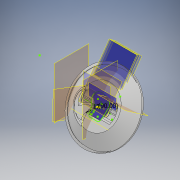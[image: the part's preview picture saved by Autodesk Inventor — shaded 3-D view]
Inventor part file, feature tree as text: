
AUTODESK INVENTOR PART (.ipt)
format: ipt  version: 2018 (Build 220112000, 112)  size: 3,591,168 bytes
history: native  units: mm
features: sketch x139, extrude x124, fillet x51, plane x14, revolve x4, hole x1, direct_edit x1, other x1
ambient origin geometry x8: Origin, YZ Plane, XZ Plane, XY Plane, X Axis, Y Axis, Z Axis, Center Point
bodies: Body1 (feature_tree)
feature tree (335):
  plane  "Work Plane5"
  sketch  "Sketch28"  dims[d118=18.7mm d119=0.0mm d120=0.9mm d121=0.0mm]
  extrude  "Extrusion21"  Depth=0.9mm TaperAngle=0.0deg
  plane  "Work Plane4"
  extrude  "Extrusion22"  Depth=3.8mm
  extrude  "Extrusion23"  Depth=46.7mm
  plane  "Work Plane3"
  hole  "Hole6"  [1 undecoded]
  extrude  "Extrusion27"  Depth=3.8mm
  extrude  "Extrusion28"  Depth=32.03mm
  extrude  "Extrusion30"  Depth=10.0mm TaperAngle=0.0deg
  extrude  "Extrusion31"  Depth=16.3mm TaperAngle=0.0deg
  sketch  "Sketch56"  dims[d188=16.3mm d189=0.0mm d190=16.3mm d191=0.0mm]
  sketch  "Sketch57"  dims[d192=16.3mm d193=0.0mm d194=16.3mm d195=0.0mm]
  extrude  "Extrusion33"  Depth=16.3mm TaperAngle=0.0deg
  extrude  "Extrusion34"  Depth=16.3mm TaperAngle=0.0deg
  extrude  "Extrusion35"  Depth=15.9mm TaperAngle=0.0deg
  extrude  "Extrusion36"  Depth=15.9mm TaperAngle=0.0deg
  extrude  "Extrusion37"  TaperAngle=90.0deg  [1 undecoded]
  extrude  "Extrusion38"  TaperAngle=0.0deg  [1 undecoded]
  extrude  "Extrusion39"  Depth=0.2mm TaperAngle=0.0deg
  extrude  "Extrusion40"  Depth=3.17mm
  extrude  "Extrusion41"  Depth=6.1mm
  sketch  "Sketch68"  dims[d251=10.0mm d252=0.0mm d253=3.91mm d254=0.0mm]
  sketch  "Sketch69"  dims[d255=0.0mm d256=0.0mm d257=3.91mm d258=0.0mm]
  extrude  "Extrusion42"  Depth=0.8mm TaperAngle=0.0deg
  extrude  "Extrusion43"  TaperAngle=0.0deg  [1 undecoded]
  extrude  "Extrusion45"  Depth=10.0mm TaperAngle=0.0deg
  extrude  "Extrusion47"  Depth=3.91mm TaperAngle=0.0deg
  extrude  "Extrusion48"  Depth=0.6mm TaperAngle=0.0deg
  extrude  "Extrusion49"  Depth=0.199mm
  direct_edit  "Direct Edit3"
  extrude  "Extrusion51"  TaperAngle=0.0deg  [1 undecoded]
  extrude  "Extrusion52"  Depth=0.7mm TaperAngle=0.0deg
  extrude  "Extrusion53"  Depth=0.09mm TaperAngle=0.0deg
  extrude  "Extrusion54"  TaperAngle=0.0deg  [1 undecoded]
  extrude  "Extrusion55"  Depth=3.9mm TaperAngle=0.0deg
  extrude  "Extrusion60"  TaperAngle=0.0deg  [1 undecoded]
  extrude  "Extrusion61"  Depth=0.657mm
  extrude  "Extrusion62"  Depth=10.0mm TaperAngle=0.0deg
  fillet  "Fillet13"  Radius=10.0mm
  extrude  "Extrusion64"  TaperAngle=0.0deg  [1 undecoded]
  extrude  "Extrusion65"  TaperAngle=0.0deg  [1 undecoded]
  extrude  "Extrusion66"  Depth=0.253mm
  extrude  "Extrusion67"  TaperAngle=0.0deg  [1 undecoded]
  fillet  "Fillet14"  [1 undecoded]
  extrude  "Extrusion68"  Depth=15.0mm
  extrude  "Extrusion69"  Depth=22.68928mm
  extrude  "Extrusion70"  TaperAngle=90.0deg  [1 undecoded]
  fillet  "Fillet15"  [1 undecoded]
  extrude  "Extrusion71"  TaperAngle=90.0deg  [1 undecoded]
  extrude  "Extrusion72"  Depth=3.490659mm
  extrude  "Extrusion73"  Depth=2.0mm TaperAngle=0.0deg
  extrude  "Extrusion74"  TaperAngle=0.0deg  [1 undecoded]
  fillet  "Fillet16"  Radius=10.0mm
  fillet  "Fillet17"  Radius=0.22mm
  extrude  "Extrusion75"  Depth=5.0mm TaperAngle=0.0deg
  plane  "Work Plane6"
  extrude  "Extrusion78"  Depth=10.0mm TaperAngle=0.0deg
  extrude  "Extrusion79"  Depth=10.0mm TaperAngle=0.0deg
  extrude  "Extrusion80"  Depth=10.0mm TaperAngle=0.0deg
  extrude  "Extrusion81"  Depth=10.0mm TaperAngle=0.0deg
  extrude  "Extrusion82"  Depth=10.0mm
  fillet  "Fillet18"  [1 undecoded]
  fillet  "Fillet19"  Radius=5.99mm
  fillet  "Fillet20"  Radius=1.49mm
  extrude  "Extrusion83"  Depth=1.77mm
  extrude  "Extrusion84"  Depth=10.0mm TaperAngle=0.0deg
  fillet  "Fillet21"  Radius=4.0mm
  extrude  "Extrusion87"  Depth=4.0mm TaperAngle=0.0deg
  plane  "Work Plane7"
  extrude  "Extrusion88"  TaperAngle=0.0deg  [1 undecoded]
  extrude  "Extrusion89"  Depth=7.0mm TaperAngle=0.0deg
  extrude  "Extrusion90"  Depth=10.0mm TaperAngle=0.0deg
  extrude  "Extrusion91"  Depth=7.0mm TaperAngle=0.0deg
  fillet  "Fillet27"  Radius=7.0mm
  extrude  "Extrusion93"  Depth=7.0mm TaperAngle=0.0deg
  extrude  "Extrusion94"  Depth=1.7mm TaperAngle=0.0deg
  fillet  "Fillet29"  [1 undecoded]
  extrude  "Extrusion95"  Depth=10.0mm TaperAngle=0.0deg
  extrude  "Extrusion97"  Depth=10.0mm TaperAngle=0.0deg
  extrude  "Extrusion98"  Depth=1.0mm TaperAngle=0.0deg
  extrude  "Extrusion99"  Depth=15.687mm
  extrude  "Extrusion100"  Depth=9.4mm
  extrude  "Extrusion101"  TaperAngle=90.0deg  [1 undecoded]
  extrude  "Extrusion102"  Depth=10.0mm TaperAngle=0.0deg
  extrude  "Extrusion104"  Depth=50.0mm TaperAngle=0.0deg
  fillet  "Fillet30"  Radius=50.0mm
  extrude  "Extrusion106"  Depth=10.0mm TaperAngle=0.0deg
  fillet  "Fillet33"  Radius=32.0mm
  fillet  "Fillet34"  Radius=9.4mm
  fillet  "Fillet35"  [1 undecoded]
  fillet  "Fillet38"  Radius=10.0mm
  extrude  "Extrusion108"  Depth=10.0mm TaperAngle=0.0deg
  extrude  "Extrusion109"  Depth=10.0mm TaperAngle=0.0deg
  extrude  "Extrusion110"  TaperAngle=0.0deg  [1 undecoded]
  extrude  "Extrusion111"  Depth=18.0mm TaperAngle=0.0deg
  extrude  "Extrusion112"  Depth=2.0mm
  sketch  "Sketch146"  dims[d571=2.0mm d572=2.0mm]
  extrude  "Extrusion113"  Depth=2.0mm
  extrude  "Extrusion114"  Depth=2.0mm
  extrude  "Extrusion115"  Depth=2.0mm
  extrude  "Extrusion116"  Depth=2.0mm
  extrude  "Extrusion118"  Depth=2.0mm
  sketch  "Sketch154"  dims[d590=2.0mm d591=4.0mm]
  extrude  "Extrusion119"  Depth=2.0mm
  extrude  "Extrusion120"  Depth=0.7mm TaperAngle=0.0deg
  extrude  "Extrusion121"  Depth=10.0mm TaperAngle=0.0deg
  extrude  "Extrusion122"  Depth=17.0mm TaperAngle=0.0deg
  extrude  "Extrusion123"  Depth=4.0mm
  extrude  "Extrusion124"  Depth=1.0mm TaperAngle=0.0deg
  extrude  "Extrusion125"  Depth=6.6945mm
  extrude  "Extrusion126"  TaperAngle=0.0deg  [1 undecoded]
  extrude  "Extrusion128"  Depth=15.2mm
  extrude  "Extrusion129"  Depth=26.0mm
  extrude  "Extrusion130"  Depth=28.5mm TaperAngle=0.0deg
  plane  "Work Plane9"
  extrude  "Extrusion133"  Depth=2.0mm
  extrude  "Extrusion134"  Depth=0.567mm
  plane  "Work Plane8"
  extrude  "Extrusion135"  Depth=0.37mm TaperAngle=0.0deg
  plane  "Work Plane2"
  revolve  "Revolution3"  [1 undecoded]
  plane  "Work Plane10"
  extrude  "Extrusion136"  Depth=2.0mm
  extrude  "Extrusion137"  Depth=2.0mm
  extrude  "Extrusion138"  TaperAngle=90.0deg  [1 undecoded]
  extrude  "Extrusion139"  Depth=0.449mm
  sketch  "Sketch184"  dims[d657=2.0mm d658=1.2mm d659=0.0mm]
  plane  "Work Plane11"
  extrude  "Extrusion140"  Depth=0.526mm
  extrude  "Extrusion141"  [1 undecoded]
  extrude  "Extrusion142"  [1 undecoded]
  extrude  "Extrusion143"  Depth=2.0mm
  revolve  "Revolution4"  [1 undecoded]
  extrude  "Extrusion145"  Depth=1.2mm TaperAngle=0.0deg
  sketch  "Sketch192"
  extrude  "Extrusion147"  Depth=2.0mm
  extrude  "Extrusion148"  Depth=1.0mm
  extrude  "Extrusion149"  [1 undecoded]
  sketch  "Sketch198"
  sketch  "Sketch199"
  sketch  "Sketch200"
  extrude  "Extrusion150"  [1 undecoded]
  sketch  "Sketch201"
  sketch  "Sketch202"
  extrude  "Extrusion151"  [1 undecoded]
  extrude  "Extrusion152"  [1 undecoded]
  extrude  "Extrusion153"  [1 undecoded]
  extrude  "Extrusion154"  [1 undecoded]
  sketch  "Sketch207"
  extrude  "Extrusion155"  [1 undecoded]
  fillet  "Fillet39"  [1 undecoded]
  fillet  "Fillet40"  [1 undecoded]
  fillet  "Fillet41"  [1 undecoded]
  fillet  "Fillet42"  [1 undecoded]
  fillet  "Fillet43"  [1 undecoded]
  fillet  "Fillet44"  [1 undecoded]
  fillet  "Fillet45"  [1 undecoded]
  fillet  "Fillet46"  [1 undecoded]
  fillet  "Fillet47"  [1 undecoded]
  plane  "Work Plane12"
  extrude  "Extrusion156"  [1 undecoded]
  fillet  "Fillet48"  [1 undecoded]
  fillet  "Fillet49"  [1 undecoded]
  fillet  "Fillet50"  [1 undecoded]
  fillet  "Fillet51"  [1 undecoded]
  extrude  "Extrusion157"  [1 undecoded]
  fillet  "Fillet52"  [1 undecoded]
  extrude  "Extrusion158"  [1 undecoded]
  extrude  "Extrusion159"  [1 undecoded]
  extrude  "Extrusion161"  [1 undecoded]
  fillet  "Fillet53"  [1 undecoded]
  plane  "Work Plane13"
  extrude  "Extrusion163"  [1 undecoded]
  extrude  "Extrusion164"  [1 undecoded]
  extrude  "Extrusion166"  [1 undecoded]
  extrude  "Extrusion167"  [1 undecoded]
  revolve  "Revolution5"  [1 undecoded]
  extrude  "Extrusion168"  [1 undecoded]
  fillet  "Fillet54"  [1 undecoded]
  fillet  "Fillet55"  [1 undecoded]
  extrude  "Extrusion169"  [1 undecoded]
  sketch  "Sketch220"
  fillet  "Fillet56"  [1 undecoded]
  fillet  "Fillet57"  [1 undecoded]
  extrude  "Extrusion171"  [1 undecoded]
  extrude  "Extrusion172"  [1 undecoded]
  fillet  "Fillet58"  [1 undecoded]
  fillet  "Fillet59"  [1 undecoded]
  fillet  "Fillet60"  [1 undecoded]
  fillet  "Fillet61"  [1 undecoded]
  fillet  "Fillet62"  [1 undecoded]
  fillet  "Fillet63"  [1 undecoded]
  revolve  "Revolution6"  [1 undecoded]
  fillet  "Fillet64"  [1 undecoded]
  extrude  "Extrusion173"  [1 undecoded]
  fillet  "Fillet65"  [1 undecoded]
  fillet  "Fillet66"  [1 undecoded]
  plane  "Work Plane14"
  extrude  "Extrusion174"  [1 undecoded]
  sketch  "Sketch225"
  plane  "Work Plane15"
  extrude  "Extrusion176"  [1 undecoded]
  fillet  "Fillet67"  [1 undecoded]
  fillet  "Fillet68"  [1 undecoded]
  fillet  "Fillet69"  [1 undecoded]
  fillet  "Fillet70"  [1 undecoded]
  extrude  "Extrusion177"  [1 undecoded]
  fillet  "Fillet71"  [1 undecoded]
  fillet  "Fillet72"  [1 undecoded]
  fillet  "Fillet73"  [1 undecoded]
  sketch  "Sketch41"  dims[d122=0.7mm d123=0.0mm d128=3.8mm]
  sketch  "Sketch42"  dims[d129=3.8mm d130=46.7mm]
  sketch  "Sketch43"  dims[d134=3.8mm d135=4.369mm d136=5.824mm d137=2.0mm d138=14.3117mm d139=6.637mm d140=0.0mm d150=1.5mm d151=0.0mm]
  sketch  "Sketch50"  dims[d152=1.2mm d153=0.0mm d159=3.8mm]
  sketch  "Sketch51"  dims[d161=3.8mm d168=23.3333mm d173=32.03mm]
  sketch  "Sketch53"  dims[d174=16.015mm d175=10.0mm d176=0.0mm]
  sketch  "Sketch54"  dims[d179=0.0mm d180=0.0mm d186=16.3mm d187=0.0mm]
  sketch  "Sketch58"  dims[d196=15.9mm d197=0.0mm d198=15.9mm d199=0.0mm]
  sketch  "Sketch60"  dims[d200=15.9mm d201=0.0mm d202=15.9mm d203=0.0mm]
  sketch  "Sketch61"  dims[d209=17.0mm d210=90.0deg]
  sketch  "Sketch62"  dims[d211=6.0mm d212=0.0mm d213=0.0mm d214=0.0mm]
  sketch  "Sketch63"  dims[d225=6.0mm d226=0.0mm d230=0.2mm d231=0.0mm]
  sketch  "Sketch64"  dims[d232=3.17mm d233=3.17mm]
  sketch  "Sketch65"  dims[d235=19.4mm d236=6.1mm]
  sketch  "Sketch66"  dims[d237=0.8mm d238=0.0mm d239=0.8mm d240=0.0mm]
  sketch  "Sketch67"  dims[d246=9.0mm d247=10.0mm d248=10.0mm d249=0.0mm d250=0.0mm]
  sketch  "Sketch70"  dims[d267=0.0mm d268=0.0mm d269=0.6mm d270=0.0mm]
  sketch  "Sketch72"  dims[d271=0.0mm d272=0.0mm d273=0.199mm]
  sketch  "Sketch74"  dims[d276=0.0mm d277=0.0mm d278=0.0mm d279=0.0mm]
  sketch  "Sketch75"  dims[d280=0.7mm d281=0.0mm d282=0.7mm d283=0.0mm]
  sketch  "Sketch76"  dims[d284=3.64mm d285=0.09mm d286=0.0mm]
  sketch  "Sketch79"  dims[d287=0.09mm d288=0.0mm d289=0.0mm d290=0.0mm]
  sketch  "Sketch80"  dims[d291=0.356mm d292=3.9mm d293=0.0mm]
  sketch  "Sketch81"  dims[d294=3.9mm d295=0.0mm d296=0.0mm d297=0.0mm]
  sketch  "Sketch82"  dims[d298=3.9mm d299=0.0mm d300=0.657mm]
  sketch  "Sketch83"  dims[d301=0.886mm d302=3.9mm d303=0.0mm d313=10.0mm d314=0.0mm]
  sketch  "Sketch89"  dims[d315=10.0mm d316=0.0mm d317=0.0mm d318=0.0mm]
  sketch  "Sketch90"  dims[d319=10.0mm d320=0.0mm d321=0.0mm d322=0.0mm]
  sketch  "Sketch91"  dims[d323=0.467mm d324=0.253mm]
  sketch  "Sketch93"  dims[d325=0.195mm d326=0.0mm d327=0.0mm d328=90.0deg]
  sketch  "Sketch94"  dims[d329=90.0deg d330=15.0mm]
  sketch  "Sketch95"  dims[d332=11.0mm d333=22.68928mm]
  sketch  "Sketch96"  dims[d335=90.0deg d336=90.0deg d337=0.0mm d338=0.0mm]
  sketch  "Sketch97"  dims[d344=0.954mm d350=90.0deg]
  sketch  "Sketch98"  dims[d351=3.490659mm d352=3.490659mm]
  sketch  "Sketch99"  dims[d353=6.0mm d354=0.0mm d363=2.0mm d364=0.0mm]
  sketch  "Sketch100"  dims[d365=2.0mm d366=0.0mm d374=0.0mm d375=0.0mm d376=10.0mm d377=0.0mm d378=0.22mm]
  sketch  "Sketch101"  dims[d381=5.0mm d382=0.0mm d383=5.0mm d384=0.0mm]
  sketch  "Sketch102"  dims[d386=3.8mm d397=10.0mm d398=0.0mm]
  sketch  "Sketch103"  dims[d401=0.3mm d402=0.0mm d403=10.0mm d404=0.0mm]
  sketch  "Sketch104"  dims[d405=10.0mm d406=0.0mm d407=10.0mm d408=0.0mm]
  sketch  "Sketch106"  dims[d409=10.0mm d410=0.0mm d411=10.0mm d412=0.0mm]
  sketch  "Sketch107"  dims[d415=10.0mm d416=0.0mm d419=0.865mm d421=0.0mm d422=0.0mm d424=5.99mm d425=1.49mm]
  sketch  "Sketch108"  dims[d426=0.859mm d431=1.77mm]
  sketch  "Sketch109"  dims[d432=10.0mm d433=0.0mm d434=4.0mm d435=0.0mm d436=4.0mm d437=0.0mm]
  sketch  "Sketch110"  dims[d438=4.0mm d439=0.0mm d440=4.0mm d441=0.0mm]
  sketch  "Sketch113"  dims[d442=0.0mm d443=0.0mm d444=0.0mm d445=0.0mm]
  sketch  "Sketch114"  dims[d446=1.0mm d447=0.0mm d448=7.0mm d449=0.0mm]
  sketch  "Sketch117"  dims[d452=7.0mm d453=0.0mm d454=10.0mm d455=0.0mm]
  sketch  "Sketch118"  dims[d456=0.0mm d457=0.0mm d458=7.0mm d459=0.0mm d460=7.0mm d461=0.0mm]
  sketch  "Sketch119"  dims[d462=0.0mm d463=0.0mm d464=7.0mm d465=0.0mm]
  sketch  "Sketch120"  dims[d466=1.7mm d467=0.0mm d468=1.7mm d469=0.0mm d483=0.0mm d484=0.0mm]
  sketch  "Sketch121"  dims[d485=0.0mm d486=0.0mm d487=10.0mm d488=0.0mm]
  sketch  "Sketch123"  dims[d496=10.0mm d497=0.0mm d498=10.0mm d499=0.0mm]
  sketch  "Sketch124"  dims[d500=31.5mm d501=1.0mm d502=0.0mm]
  sketch  "Sketch126"  dims[d508=-1.0mm d509=15.687mm]
  sketch  "Sketch128"  dims[d510=90.0deg d514=9.4mm]
  sketch  "Sketch129"  dims[d516=7.0mm d519=90.0deg]
  sketch  "Sketch130"  dims[d520=2.75mm d521=0.0mm d522=10.0mm d523=0.0mm]
  sketch  "Sketch131"  dims[d524=7.0mm d525=0.0mm d527=50.0mm d528=0.0mm d529=50.0mm d530=0.0mm]
  sketch  "Sketch132"  dims[d531=50.0mm d532=0.0mm d533=50.0mm d534=0.0mm d535=32.0mm d536=0.0mm d537=9.4mm d538=7.0mm d539=90.0deg d542=10.0mm d543=0.0mm]
  sketch  "Sketch133"  dims[d546=10.0mm d547=0.0mm d548=10.0mm d549=0.0mm]
  sketch  "Sketch135"  dims[d550=31.0mm d551=0.0mm d552=10.0mm d553=0.0mm]
  sketch  "Sketch137"  dims[d554=5.5mm d555=0.0mm d556=0.0mm d557=0.0mm]
  sketch  "Sketch141"  dims[d558=5.5mm d559=0.0mm d560=18.0mm d561=0.0mm]
  sketch  "Sketch142"  dims[d562=18.0mm d563=0.0mm d564=2.0mm]
  sketch  "Sketch143"  dims[d565=2.0mm d566=2.0mm]
  sketch  "Sketch144"  dims[d567=2.0mm d568=2.0mm]
  sketch  "Sketch145"  dims[d569=2.0mm d570=2.0mm]
  sketch  "Sketch147"  dims[d573=0.0mm d574=0.0mm d575=2.0mm]
  sketch  "Sketch148"  dims[d576=2.0mm d577=2.0mm]
  sketch  "Sketch149"  dims[d578=2.0mm d579=0.7mm d580=0.0mm]
  sketch  "Sketch150"  dims[d581=2.0mm d582=10.0mm d583=0.0mm]
  sketch  "Sketch153"  dims[d584=2.15mm d585=0.0mm d588=17.0mm d589=0.0mm]
  sketch  "Sketch156"  dims[d594=3.0mm d595=0.0mm d596=1.0mm d597=0.0mm]
  sketch  "Sketch157"  dims[d598=7.23mm d599=6.6945mm]
  sketch  "Sketch161"  dims[d602=31.423mm d603=0.0mm d604=0.0mm]
  sketch  "Sketch162"  dims[d605=1.0mm d606=0.0mm d607=15.2mm]
  sketch  "Sketch163"  dims[d609=5.093mm d611=26.0mm]
  sketch  "Sketch164"  dims[d615=90.0deg d616=28.5mm d617=0.0mm]
  sketch  "Sketch165"  dims[d618=2.0mm d619=2.0mm]
  sketch  "Sketch166"  dims[d620=2.235mm d621=0.0mm d624=0.567mm]
  sketch  "Sketch169"  dims[d625=0.682mm d626=0.37mm d627=0.0mm]
  sketch  "Sketch170"  dims[d628=1.2mm d629=0.0mm d630=2.0mm]
  sketch  "Sketch171"  dims[d631=2.0mm d632=2.0mm]
  sketch  "Sketch174"  dims[d633=2.0mm d634=2.0mm]
  sketch  "Sketch175"  dims[d635=2.0mm d639=90.0deg]
  sketch  "Sketch176"  dims[d640=90.0deg d641=0.449mm]
  sketch  "Sketch179"  dims[d642=1.2mm d643=0.0mm d644=0.526mm]
  sketch  "Sketch180"  dims[d645=2.0mm d646=-23.0mm]
  sketch  "Sketch181"  dims[d647=18.0mm d648=0.0mm d651=-2.2mm]
  sketch  "Sketch182"  dims[d652=1.4mm d653=0.0mm d654=2.0mm]
  sketch  "Sketch183"  dims[d655=2.0mm d656=2.0mm]
  sketch  "Sketch185"  dims[d660=2.0mm d661=2.0mm]
  sketch  "Sketch186"  dims[d662=2.0mm d21=1.0mm]
  sketch  "Sketch187"  dims[d22=1.0mm]
  sketch  "Sketch188"
  sketch  "Sketch190"
  sketch  "Sketch193"
  sketch  "Sketch194"
  sketch  "Sketch195"
  sketch  "Sketch204"
  sketch  "Sketch205"
  sketch  "Sketch206"
  sketch  "Sketch208"
  sketch  "Sketch209"
  sketch  "Sketch210"
  sketch  "Sketch211"
  sketch  "Sketch212"
  sketch  "Sketch213"
  sketch  "Sketch214"
  sketch  "Sketch215"
  sketch  "Sketch216"
  sketch  "Sketch217"
  sketch  "Sketch218"
  sketch  "Sketch219"
  sketch  "Sketch221"
  sketch  "Sketch222"
  sketch  "Sketch223"
  sketch  "Sketch224"
  sketch  "Sketch226"
  sketch  "Sketch227"
  other  "Scale3"
note: 88 required parameter values undecoded (feature->parameter linkage not recoverable at this tier; creation-order binding heuristic only, values carry confidence <= 0.55)